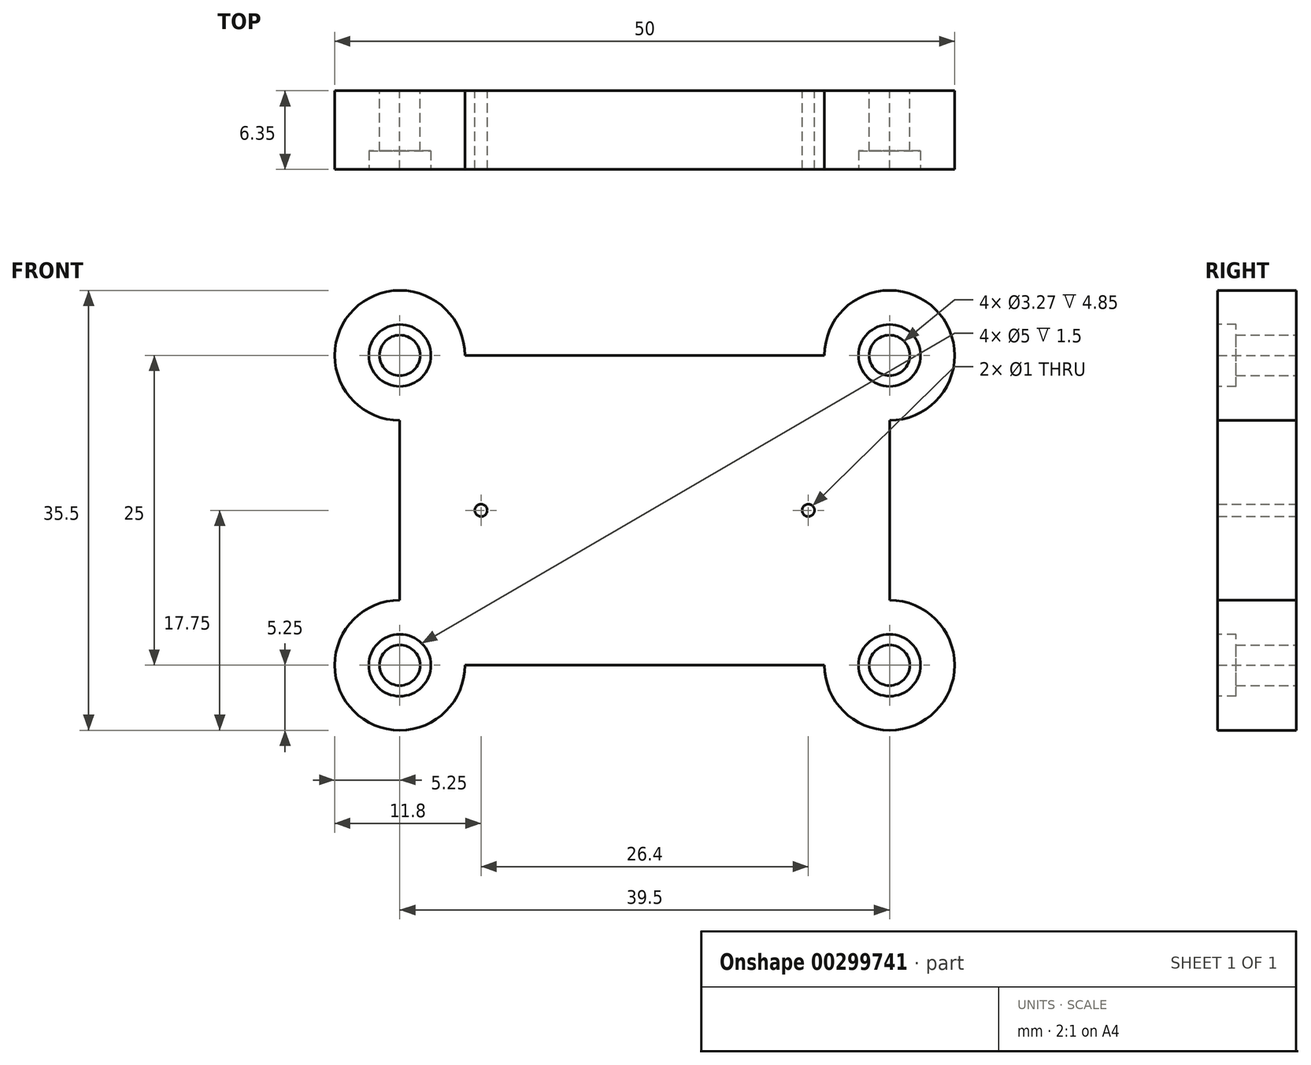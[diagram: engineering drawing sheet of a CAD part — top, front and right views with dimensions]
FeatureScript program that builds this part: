
annotation { "Feature Type Name" : "Feature", "Feature Type Description" : "" }
export const myFeature = defineFeature(function(context is Context, id is Id, definition is map)
    precondition{}
    {
        {
            var Q0;
            Q0=qCreatedBy(makeId("Front.planeOp"),FACE);
            var sketch = newSketch(context, id + "F0", { "sketchPlane" : qUnion([Q0])});
            skLineSegment(sketch, "E0.bottom", {"start": v(0, 0) * mm, "end": v(39.5, 0) * mm});
            skLineSegment(sketch, "E0.top", {"start": v(0, 25) * mm, "end": v(39.5, 25) * mm});
            skLineSegment(sketch, "E0.left", {"start": v(0, 0) * mm, "end": v(0, 25) * mm});
            skLineSegment(sketch, "E0.right", {"start": v(39.5, 0) * mm, "end": v(39.5, 25) * mm});
            skCircle(sketch, "E1", {"center": v(39.5, 25) * mm, "radius": 1.63 * mm});
            skCircle(sketch, "E2", {"center": v(39.5, 0) * mm, "radius": 1.64 * mm});
            skCircle(sketch, "E3", {"center": v(0, 0) * mm, "radius": 1.64 * mm});
            skCircle(sketch, "E4", {"center": v(0, 25) * mm, "radius": 1.64 * mm});
            skCircle(sketch, "E5", {"center": v(39.5, 25) * mm, "radius": 5.25 * mm});
            skCircle(sketch, "E6", {"center": v(39.5, 0) * mm, "radius": 5.25 * mm});
            skCircle(sketch, "E7", {"center": v(0, 0) * mm, "radius": 5.25 * mm});
            skCircle(sketch, "E8", {"center": v(0, 25) * mm, "radius": 5.25 * mm});
            skSolve(sketch);
        }
        {
            var Q0;
            Q0 = qSketchRegion(id + "F0", true);
            extrude(context, id + "F1", {"entities" : qUnion([Q0]), "depth" : 6.35 * mm});
        }
        {
            var Q0;
            Q0=makeQuery(id+"F1.opExtrude","CAP_FACE",FACE,{"disambiguationData":[OSD([sQuery(id+"F0.wireOp",EDGE,"E0.bottom"),sQuery(id+"F0.wireOp",EDGE,"E0.top"),sQuery(id+"F0.wireOp",EDGE,"E0.left"),sQuery(id+"F0.wireOp",EDGE,"E0.right"),sQuery(id+"F0.wireOp",EDGE,"E1"),sQuery(id+"F0.wireOp",EDGE,"E2"),sQuery(id+"F0.wireOp",EDGE,"E3"),sQuery(id+"F0.wireOp",EDGE,"E4"),sQuery(id+"F0.wireOp",EDGE,"E5"),sQuery(id+"F0.wireOp",EDGE,"E6"),sQuery(id+"F0.wireOp",EDGE,"E7"),sQuery(id+"F0.wireOp",EDGE,"E8")])],"isStart":false});
            var sketch = newSketch(context, id + "F2", { "sketchPlane" : qUnion([Q0])});
            skCircle(sketch, "E9", {"center": v(0, 25) * mm, "radius": 2.5 * mm});
            skCircle(sketch, "E10", {"center": v(39.5, 25) * mm, "radius": 2.5 * mm});
            skCircle(sketch, "E11", {"center": v(39.5, 0) * mm, "radius": 2.5 * mm});
            skCircle(sketch, "E12", {"center": v(0, 0) * mm, "radius": 2.5 * mm});
            skSolve(sketch);
        }
        {
            var Q0;
            Q0 = qSketchRegion(id + "F2", true);
            extrude(context, id + "F3", {"entities" : qUnion([Q0]), "operationType" : NewBodyOperationType.REMOVE, "oppositeDirection" : true, "depth" : 1.5 * mm});
        }
        {
            var Q0;
            Q0=makeQuery(id+"F1.opExtrude","CAP_FACE",FACE,{"disambiguationData":[OSD([sQuery(id+"F0.wireOp",EDGE,"E0.bottom"),sQuery(id+"F0.wireOp",EDGE,"E0.top"),sQuery(id+"F0.wireOp",EDGE,"E0.left"),sQuery(id+"F0.wireOp",EDGE,"E0.right"),sQuery(id+"F0.wireOp",EDGE,"E1"),sQuery(id+"F0.wireOp",EDGE,"E2"),sQuery(id+"F0.wireOp",EDGE,"E3"),sQuery(id+"F0.wireOp",EDGE,"E4"),sQuery(id+"F0.wireOp",EDGE,"E5"),sQuery(id+"F0.wireOp",EDGE,"E6"),sQuery(id+"F0.wireOp",EDGE,"E7"),sQuery(id+"F0.wireOp",EDGE,"E8")])],"isStart":true});
            var sketch = newSketch(context, id + "F4", { "sketchPlane" : qUnion([Q0])});
            skLineSegment(sketch, "E13", {"start": v(-19.75, 25) * mm, "end": v(-19.75, 0) * mm});
            skLineSegment(sketch, "E14", {"start": v(-32.95, 12.5) * mm, "end": v(-6.55, 12.5) * mm});
            skCircle(sketch, "E15", {"center": v(-32.95, 12.5) * mm, "radius": 3.45 * mm});
            skCircle(sketch, "E16", {"center": v(-6.55, 12.5) * mm, "radius": 3.45 * mm});
            skPoint(sketch, "E17", {"position": v(-19.75, 12.5) * mm});
            skCircle(sketch, "E18", {"center": v(-32.95, 12.5) * mm, "radius": 0.5 * mm});
            skCircle(sketch, "E19", {"center": v(-6.55, 12.5) * mm, "radius": 0.5 * mm});
            skSolve(sketch);
        }
        {
            var Q0;
            Q0=makeQuery(id+"F4.imprint","IMPRINT",FACE,{"disambiguationData":[TD([[makeQuery(id+"F4.imprint","IMPRINT",EDGE,{"derivedFrom":sQuery(id+"F4.wireOp",EDGE,"E18")}),1.0]])]});
            var Q1;
            Q1=makeQuery(id+"F4.imprint","IMPRINT",FACE,{"disambiguationData":[TD([[makeQuery(id+"F4.imprint","IMPRINT",EDGE,{"derivedFrom":sQuery(id+"F4.wireOp",EDGE,"E19")}),1.0]])]});
            extrude(context, id + "F5", {"entities" : qUnion([Q0, Q1]), "operationType" : NewBodyOperationType.REMOVE, "oppositeDirection" : true, "depth" : 25.4 * mm});
        }
    });
